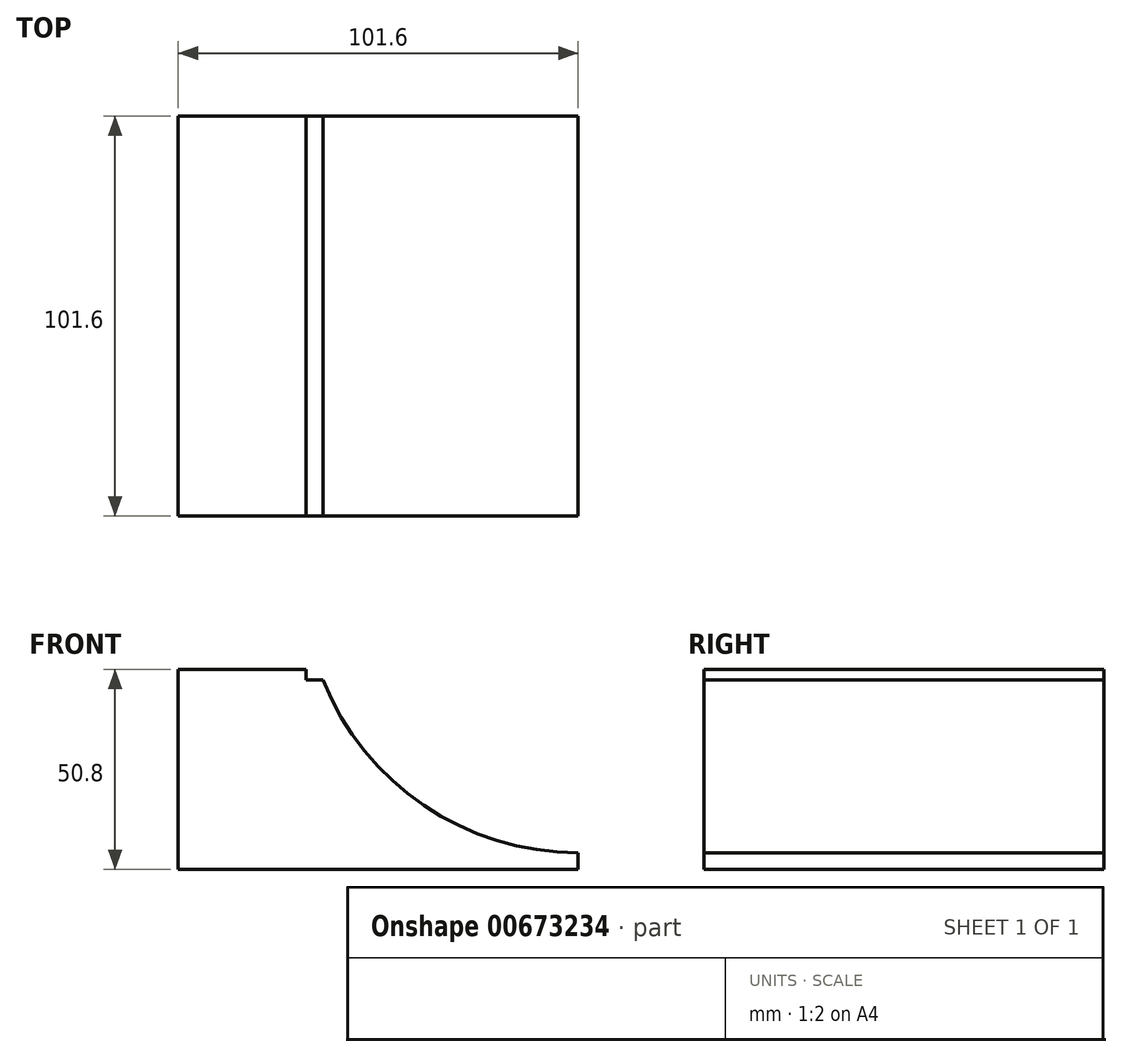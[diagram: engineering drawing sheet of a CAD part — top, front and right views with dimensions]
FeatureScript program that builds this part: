
annotation { "Feature Type Name" : "Feature", "Feature Type Description" : "" }
export const myFeature = defineFeature(function(context is Context, id is Id, definition is map)
    precondition{}
    {
        {
            var Q0;
            Q0=qCreatedBy(makeId("Front.planeOp"),FACE);
            var sketch = newSketch(context, id + "F0", { "sketchPlane" : qUnion([Q0])});
            skLineSegment(sketch, "E0.bottom", {"start": v(101.6, -50.8) * mm, "end": v(-101.6, -50.8) * mm, "construction": true});
            skLineSegment(sketch, "E0.top", {"start": v(101.6, 50.8) * mm, "end": v(-101.6, 50.8) * mm, "construction": true});
            skLineSegment(sketch, "E0.left", {"start": v(101.6, -50.8) * mm, "end": v(101.6, 50.8) * mm, "construction": true});
            skLineSegment(sketch, "E0.right", {"start": v(-101.6, -50.8) * mm, "end": v(-101.6, 50.8) * mm, "construction": true});
            skPoint(sketch, "E0.middle", {"position": v(0, 0) * mm});
            skArc(sketch, "E1", {"start": v(0, -46.57) * mm, "mid": v(-40.33, -33.75) * mm, "end": v(-65.86, 0) * mm, "construction": true});
            skPoint(sketch, "E2", {"position": v(0, -50.8) * mm});
            skLineSegment(sketch, "E3", {"start": v(-65.86, 0) * mm, "end": v(-101.6, 0) * mm, "construction": true});
            skLineSegment(sketch, "E4", {"start": v(0, -46.57) * mm, "end": v(0, -50.8) * mm});
            skLineSegment(sketch, "E5", {"start": v(-69.1, 0) * mm, "end": v(-69.1, -2.65) * mm});
            skLineSegment(sketch, "E6", {"start": v(-69.1, -2.65) * mm, "end": v(-64.86, -2.65) * mm});
            skCircle(sketch, "E7", {"center": v(-66.98, -0.53) * mm, "radius": 2.12 * mm, "construction": true});
            skLineSegment(sketch, "E8", {"start": v(-69.1, 0) * mm, "end": v(-101.6, 0) * mm});
            skLineSegment(sketch, "E9", {"start": v(-101.6, 0) * mm, "end": v(-101.6, -50.8) * mm});
            skLineSegment(sketch, "E10", {"start": v(-101.6, -50.8) * mm, "end": v(0, -50.8) * mm});
            skArc(sketch, "E11", {"start": v(0, -46.57) * mm, "mid": v(-39.17, -34.55) * mm, "end": v(-64.86, -2.65) * mm});
            skLineSegment(sketch, "E12", {"start": v(0, -48.68) * mm, "end": v(-8.47, -48.68) * mm, "construction": true});
            skPoint(sketch, "E13", {"position": v(-6.35, -48.68) * mm});
            skPoint(sketch, "E14", {"position": v(-2.12, -48.68) * mm});
            skLineSegment(sketch, "E15", {"start": v(-27.73, -36.19) * mm, "end": v(-29.52, -40.02) * mm, "construction": true});
            skLineSegment(sketch, "E16", {"start": v(-53.5, -21.62) * mm, "end": v(-59.99, -27.05) * mm, "construction": true});
            skPoint(sketch, "E17", {"position": v(-55.13, -22.98) * mm});
            skPoint(sketch, "E18", {"position": v(-58.37, -25.7) * mm});
            skPoint(sketch, "E19", {"position": v(-30.41, -41.93) * mm});
            skPoint(sketch, "E20", {"position": v(-32.2, -45.78) * mm});
            skLineSegment(sketch, "E21", {"start": v(-69.07, 2.64) * mm, "end": v(-66.18, -5.3) * mm, "construction": true});
            skLineSegment(sketch, "E22", {"start": v(-67.63, -1.33) * mm, "end": v(-65.64, -0.6) * mm, "construction": true});
            skPoint(sketch, "E23", {"position": v(-66.9, -3.32) * mm});
            skPoint(sketch, "E24", {"position": v(-68.35, 0.66) * mm});
            skSolve(sketch);
        }
        {
            var Q0;
            Q0 = qSketchRegion(id + "F0", true);
            var Q1;
            Q1 = qConstructionFilter(qBodyType(qCreatedBy(id + "F0" ,EDGE), BodyType.WIRE), ConstructionObject.NO);
            extrude(context, id + "F1", {"entities" : qUnion([Q0]), "surfaceEntities" : qUnion([Q1]), "depth" : 101.6 * mm, "offsetDistance" : 25.4 * mm});
        }
    });
